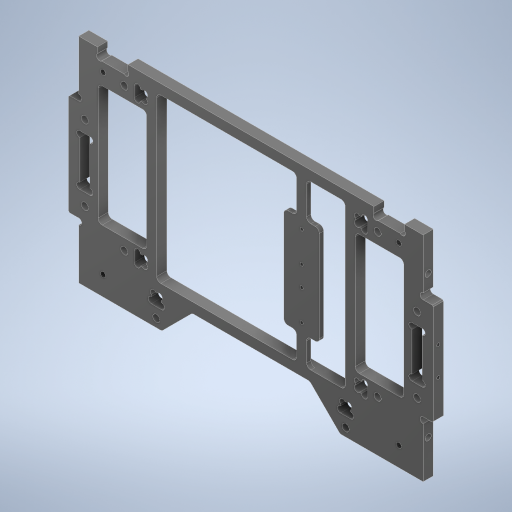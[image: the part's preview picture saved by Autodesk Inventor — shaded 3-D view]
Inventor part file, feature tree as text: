
AUTODESK INVENTOR PART (.ipt)
format: ipt  version: 2024.2 (Build 282272000, 272)  size: 663,040 bytes
history: native  units: mm
features: other x3, sketch x3, extrude x3, hole x2, mirror x1, fillet x1
ambient origin geometry x8: Origin, YZ Plane, XZ Plane, XY Plane, X Axis, Y Axis, Z Axis, Center Point
bodies: Solid1 (feature_tree)
feature tree (13):
  other  "TorsoCoverFrameBasis.ipt"
  sketch  "Sketch2"  dims[d2=25.0mm d3=1.5mm]
  extrude  "Extrusion1"  Depth=5.0mm
  hole  "Hole1"  [1 undecoded]
  mirror  "Mirror1"
  sketch  "Sketch3"  dims[d4=0.05mm d5=0.05mm d6=5.0mm d7=0.05mm d8=15.0mm d9=22.5mm d10=5.5mm d11=15.0mm d12=5.0mm d13=6.0mm d14=0.05mm d15=0.05mm d16=103.0mm d17=90.5mm d18=10.0mm d19=4.0mm d20=5.5mm d21=6.5mm d22=0.5mm d23=2.5mm d24=3.0mm d25=5.0mm d26=15.0mm d27=6.0mm d28=4.0mm d29=0.05mm d31=0.05mm d32=5.0mm d33=5.0mm d38=0.0mm d39=0.0mm d40=3.5mm d41=6.0mm d42=6.5mm d43=2.5mm d44=90.0deg d45=8.0mm d46=20.594885mm d49=2.0mm d50=6.0mm d52=58.0mm d53=88.0mm d54=0.0mm d55=15.0mm d56=2.3mm d57=88.0mm d58=20.0mm d59=17.5mm d60=15.0mm d61=35.0mm d62=25.0mm d64=17.5mm d66=60.0mm d67=2.0mm d68=5.0mm d69=2.0mm d70=0.0mm d71=2.0mm d72=1.567mm d73=4.0mm d74=4.0mm d75=2.0mm d76=90.0deg d77=6.0mm d78=0.0mm d80=2.9mm d81=0.0mm d82=0.1mm d83=0.5mm d84=0.872665mm d85=0.5mm d86=0.872665mm]
  extrude  "Extrusion3"  Depth=0.05mm
  extrude  "Extrusion4"  Depth=5.0mm
  fillet  "R2-1"  Radius=0.05mm
  hole  "Hole2"  [1 undecoded]
  other  "Solid1::TorsoCoverFrameBasis.ipt"
  other  "TaggingFeature1"
  sketch  "Sketch1"  dims[d0=10.0mm d1=5.0mm]
note: 2 required parameter values undecoded (feature->parameter linkage not recoverable at this tier; creation-order binding heuristic only, values carry confidence <= 0.55)
